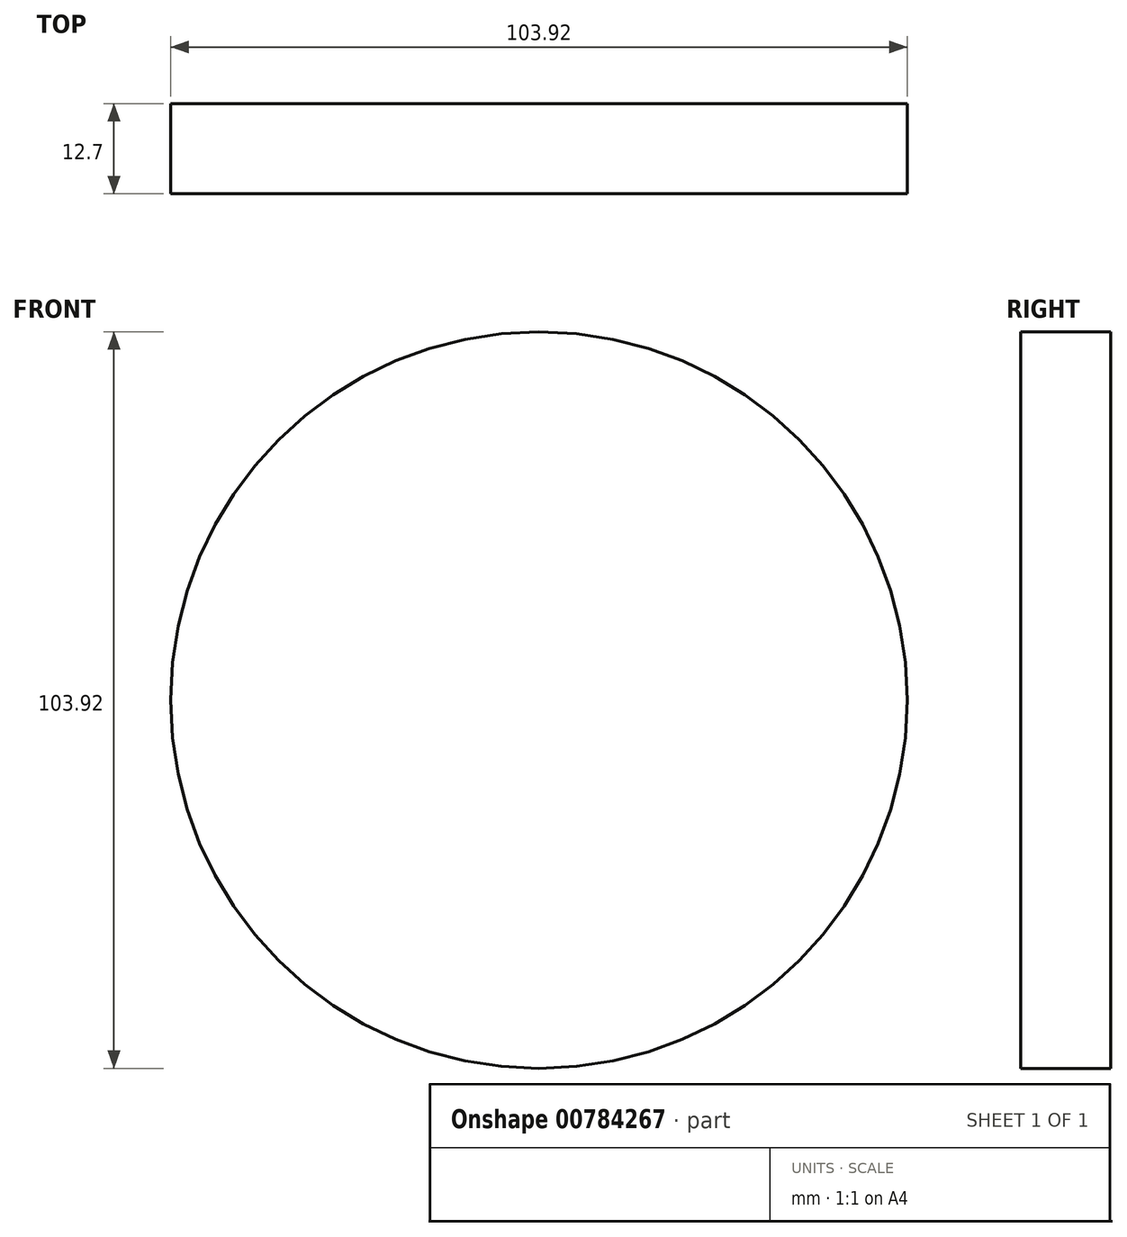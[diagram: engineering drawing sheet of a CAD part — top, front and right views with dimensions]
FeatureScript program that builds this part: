
annotation { "Feature Type Name" : "Feature", "Feature Type Description" : "" }
export const myFeature = defineFeature(function(context is Context, id is Id, definition is map)
    precondition{}
    {
        {
            var Q0;
            Q0=qCreatedBy(makeId("Front.planeOp"),FACE);
            var sketch = newSketch(context, id + "F0", { "sketchPlane" : qUnion([Q0])});
            skCircle(sketch, "E0", {"center": v(0, 0) * mm, "radius": 51.96 * mm});
            skSolve(sketch);
        }
        {
            var Q0;
            Q0 = qSketchRegion(id + "F0", true);
            extrude(context, id + "F1", {"entities" : qUnion([Q0]), "depth" : 12.7 * mm, "offsetDistance" : 25.4 * mm, "symmetric" : true});
        }
    });
